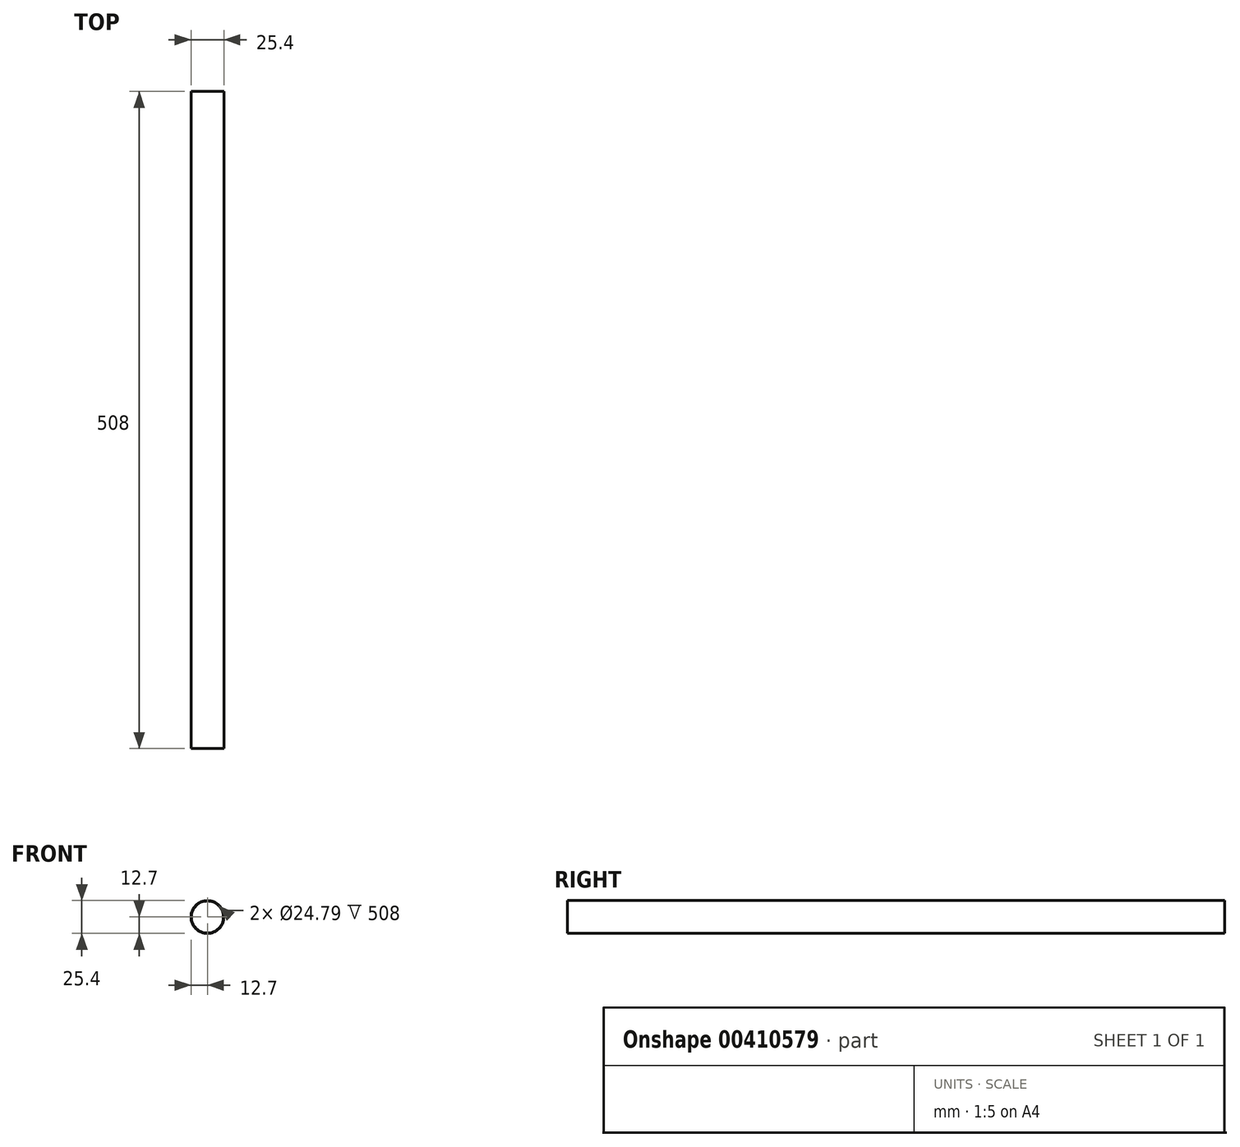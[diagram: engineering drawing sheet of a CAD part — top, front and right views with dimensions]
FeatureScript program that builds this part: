
annotation { "Feature Type Name" : "Feature", "Feature Type Description" : "" }
export const myFeature = defineFeature(function(context is Context, id is Id, definition is map)
    precondition{}
    {
        {
            var Q0;
            Q0=qCreatedBy(makeId("Front.planeOp"),FACE);
            var sketch = newSketch(context, id + "F0", { "sketchPlane" : qUnion([Q0])});
            skCircle(sketch, "E0", {"center": v(0, 0) * mm, "radius": 12.7 * mm});
            skCircle(sketch, "E1", {"center": v(0, 0) * mm, "radius": 12.4 * mm});
            skSolve(sketch);
        }
        {
            var Q0;
            Q0=qSketchRegion(id+"F0",true);
            extrude(context, id + "F1", {"entities" : qUnion([Q0]), "depth" : 508 * mm});
        }
    });
